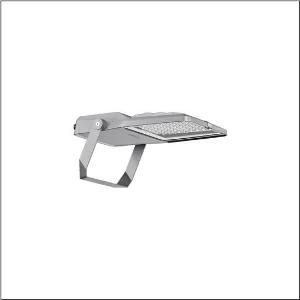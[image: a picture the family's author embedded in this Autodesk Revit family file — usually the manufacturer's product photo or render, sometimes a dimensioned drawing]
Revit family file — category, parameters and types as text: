
# Revit family: floodlight_fl_21_iq_mini___pl33t_5xa7772c4f1a_48c1
name_source: partatom
category: Lighting Fixtures
units: mm (PartAtom-declared; Revit-internal decimal feet)

## family parameters
Cut with Voids When Loaded = No
Host = Face
Light Source = No
Part Type = Normal
Room Calculation Point = No
Round Connector Dimension = Use Diameter
Shared = No

## types (1)
- --- (1 x LED, 12570 lm, 87.2 W, 4000K)
    Apparent Load = 87 VA
    CIE Flux Codes = 26 75 99 100 100
    Color Rendering = 70
    Color Temperature = 4000K
    Default Elevation = 1800 mm
    Description = Floodlight FL 21 iQ mini, floodlight, primary light control with lens, of PMMA, primary optical cover: protective disc, of toughened safety glass, transparent, light distribution: PL33T, light emission: direct distribution, installation type: surface-mounted, LED, High Power LED, rated luminous flux: 12.570lm, luminous efficacy: 144lm/W, light colour: 740, colour temperature: 4000K, control: Street-Remote, Auto-Match, Temp-Guard, Night-Set, Smart-Wire, Desk-Remote (wireless, voltage-free reading and setting of iQ features in the workshop via application-optimized NFC function/RFID function), optimised constant luminous flux control (CLO 2.0), with terminal, 6-pole, mains connection: 220..240V, AC, 50/60Hz, start of lifetime: 87W, end of service life: 92W, reduction: 40W, luminaire housing, of diecast aluminium, powder-coated, Siteco® metallic grey (DB 702S), corrosivity category C5 mid according to DIN EN ISO 12944, sealing non-destructively replaceable, mounting bracket, of steel, galvanised, powder-coated, Siteco® metallic grey (DB 702S), protection rating (complete): IP66, insulation class (complete): insulation class II (safety insulation), certification: CE, ENEC, VDE, protection symbol: D, impact resistance: IK08, permissible operating ambient temperature: -40..+40°C, permissible operating ambient temperature for outdoor applications: -40..+50°C, standard: DIN EN 12944, LABS conformity tested according to VDMA 24364:2018-05, packaging unit: 1 piece

Light Distribution: PL33T
    Height = 70 mm
    Lamp = 1 x LED
    Lamp Light Flux = 12570 lm
    Lamp Power = 87.2 W
    Lamp count = 1
    Length = 485 mm
    Luminous efficacy = 144 lm/W
    Manufacturer = Siteco
    ModVariant = No
    Model = 5XA7772C4F1A
    Number of Poles = 1
    OnlyDefault = Yes
    Power Factor = 1
    Product Name = Floodlight FL 21 iQ mini | PL33T
    Product group = floodlight | pylon annexe
    ProductGroupID = 6200
    Protection Class = Protection class II
    Protection Degree = IP 66
    RLX_Detail_Level = 1
    RLX_Emergency_Light_Flux = 0 lm
    RLX_Emergency_Type = 0
    RLX_Emergency_Type_DB = No
    RlxData = <blob elided: 96141 chars, md5=56856722>
    Socket = socket
    Standby Power = 0 W
    System Light Flux = 12570 lm
    System Power = 87 W
    Type Comments = factory setting: luminous flux: 100 % | dim-lin: 254 | 456 mA
    Type Image = l_1006845.jpg
    URL = http://relux.com
    VarID = @adj_099577
    Voltage = 0 V
    Weight = 0.00 kg
    Width = 337 mm

## geometry (parser evidence)
native form markers: Blend x4, Sweep x11
no freeform markers — native parametric forms only
